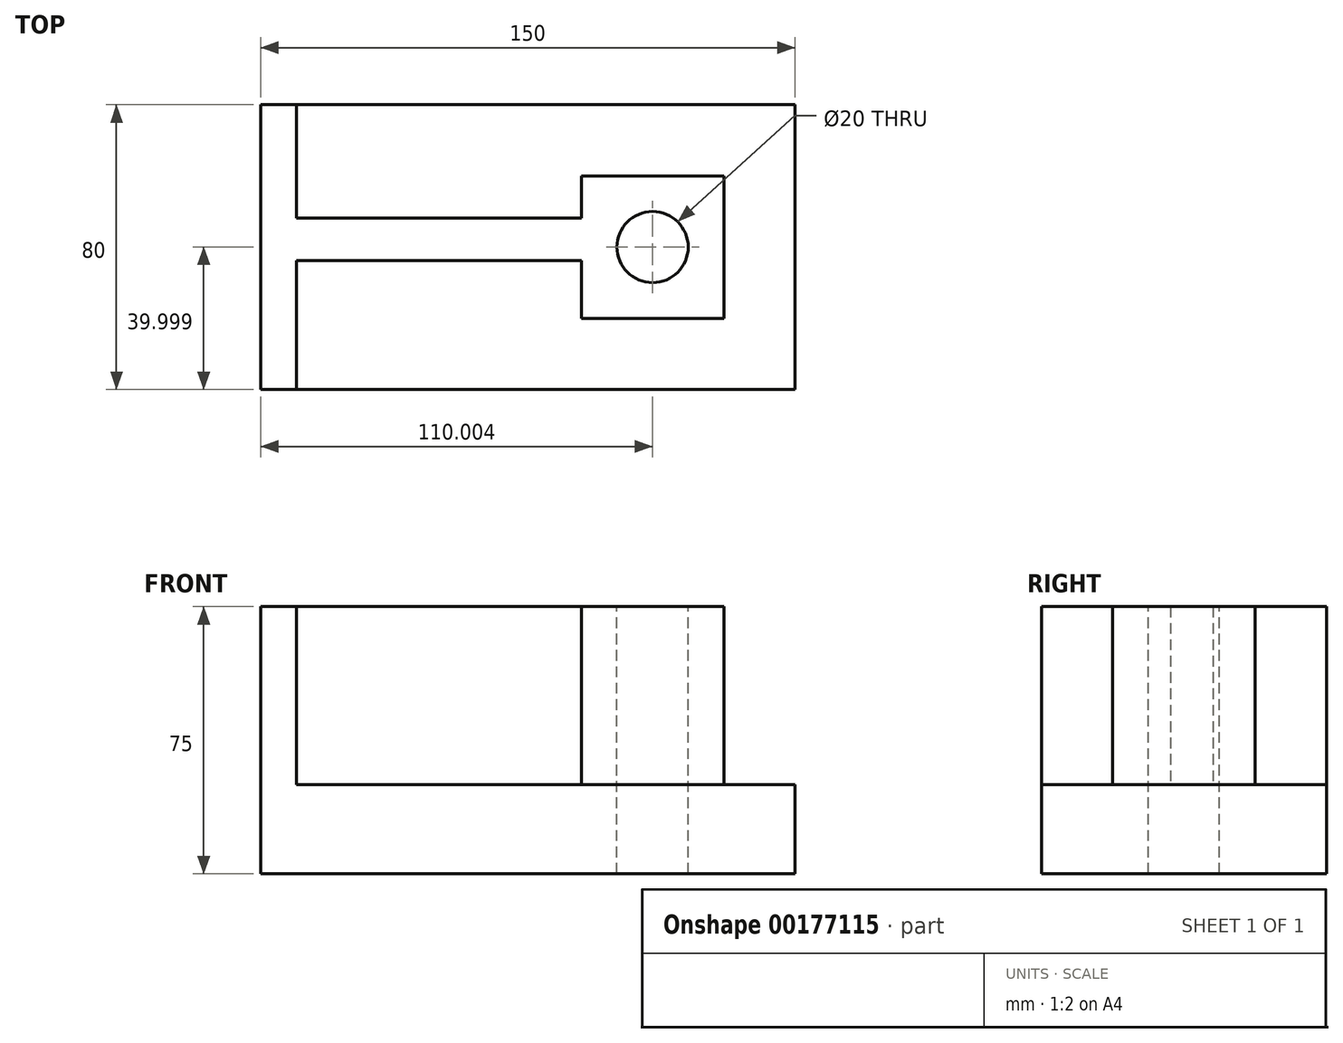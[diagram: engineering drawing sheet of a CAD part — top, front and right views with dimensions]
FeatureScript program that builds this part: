
annotation { "Feature Type Name" : "Feature", "Feature Type Description" : "" }
export const myFeature = defineFeature(function(context is Context, id is Id, definition is map)
    precondition{}
    {
        {
            var Q0;
            Q0=qCreatedBy(makeId("Top.planeOp"),FACE);
            var sketch = newSketch(context, id + "F0", { "sketchPlane" : qUnion([Q0])});
            skLineSegment(sketch, "E0.bottom", {"start": v(-84.32, -48.18) * mm, "end": v(65.68, -48.18) * mm});
            skLineSegment(sketch, "E0.top", {"start": v(-84.32, 31.82) * mm, "end": v(65.68, 31.82) * mm});
            skLineSegment(sketch, "E0.left", {"start": v(-84.32, -48.18) * mm, "end": v(-84.32, 31.82) * mm});
            skLineSegment(sketch, "E0.right", {"start": v(65.68, -48.18) * mm, "end": v(65.68, 31.82) * mm});
            skSolve(sketch);
        }
        {
            var Q0;
            Q0 = qSketchRegion(id + "F0", true);
            extrude(context, id + "F1", {"entities" : qUnion([Q0]), "depth" : 25 * mm});
        }
        {
            var Q0;
            Q0=makeQuery(id+"F1.opExtrude","CAP_FACE",FACE,{"disambiguationData":[OSD([sQuery(id+"F0.wireOp",EDGE,"E0.bottom"),sQuery(id+"F0.wireOp",EDGE,"E0.top"),sQuery(id+"F0.wireOp",EDGE,"E0.left"),sQuery(id+"F0.wireOp",EDGE,"E0.right")])],"isStart":false});
            var sketch = newSketch(context, id + "F2", { "sketchPlane" : qUnion([Q0])});
            skLineSegment(sketch, "E1", {"start": v(45.68, 11.82) * mm, "end": v(5.68, 11.82) * mm});
            skLineSegment(sketch, "E2", {"start": v(5.68, 11.82) * mm, "end": v(5.68, -28.18) * mm});
            skLineSegment(sketch, "E3", {"start": v(5.68, -28.18) * mm, "end": v(45.68, -28.18) * mm});
            skLineSegment(sketch, "E4", {"start": v(45.68, -28.18) * mm, "end": v(45.68, 11.82) * mm});
            skSolve(sketch);
        }
        {
            var Q0;
            Q0=makeQuery(id+"F2.imprint","IMPRINT",FACE,{"disambiguationData":[TD([[makeQuery(id+"F2.imprint","IMPRINT",EDGE,{"derivedFrom":sQuery(id+"F2.wireOp",EDGE,"E1")}),1.0]])]});
            extrude(context, id + "F3", {"entities" : qUnion([Q0]), "operationType" : NewBodyOperationType.ADD, "depth" : 50 * mm});
        }
        {
            var Q0;
            Q0=makeQuery(id+"F3.opExtrude","CAP_FACE",FACE,{"disambiguationData":[OSD([sQuery(id+"F2.wireOp",EDGE,"E1"),sQuery(id+"F2.wireOp",EDGE,"E2"),sQuery(id+"F2.wireOp",EDGE,"E3"),sQuery(id+"F2.wireOp",EDGE,"E4")])],"isStart":false});
            var sketch = newSketch(context, id + "F4", { "sketchPlane" : qUnion([Q0])});
            skCircle(sketch, "E5", {"center": v(25.68, -8.18) * mm, "radius": 10 * mm});
            skPoint(sketch, "E6.end.orphan", {"position": v(45.68, -8.18) * mm});
            skSolve(sketch);
        }
        {
            var Q0;
            Q0=makeQuery(id+"F4.imprint","IMPRINT",FACE,{"disambiguationData":[TD([[makeQuery(id+"F4.imprint","IMPRINT",EDGE,{"derivedFrom":sQuery(id+"F4.wireOp",EDGE,"E5")}),1.0]])]});
            extrude(context, id + "F5", {"entities" : qUnion([Q0]), "operationType" : NewBodyOperationType.REMOVE, "oppositeDirection" : true, "depth" : 75 * mm});
        }
        {
            var Q0;
            Q0=makeQuery(id+"F1.opExtrude","CAP_FACE",FACE,{"disambiguationData":[OSD([sQuery(id+"F0.wireOp",EDGE,"E0.bottom"),sQuery(id+"F0.wireOp",EDGE,"E0.top"),sQuery(id+"F0.wireOp",EDGE,"E0.left"),sQuery(id+"F0.wireOp",EDGE,"E0.right")])],"isStart":false});
            var sketch = newSketch(context, id + "F6", { "sketchPlane" : qUnion([Q0])});
            skLineSegment(sketch, "E7", {"start": v(-74.32, 0) * mm, "end": v(-74.32, -12) * mm});
            skLineSegment(sketch, "E8", {"start": v(-74.32, -12) * mm, "end": v(5.68, -12) * mm});
            skLineSegment(sketch, "E9", {"start": v(5.68, -12) * mm, "end": v(5.68, -8.18) * mm});
            skLineSegment(sketch, "E10", {"start": v(-74.32, 0) * mm, "end": v(5.68, 0) * mm});
            skSolve(sketch);
        }
        {
            var Q0;
            Q0=makeQuery(id+"F6.imprint","IMPRINT",FACE,{"disambiguationData":[TD([[makeQuery(id+"F6.imprint","IMPRINT",EDGE,{"derivedFrom":sQuery(id+"F6.wireOp",EDGE,"E7")}),1.0]])]});
            extrude(context, id + "F7", {"entities" : qUnion([Q0]), "operationType" : NewBodyOperationType.ADD, "depth" : 50 * mm});
        }
        {
            var Q0;
            Q0=makeQuery(id+"F1.opExtrude","CAP_FACE",FACE,{"disambiguationData":[OSD([sQuery(id+"F0.wireOp",EDGE,"E0.bottom"),sQuery(id+"F0.wireOp",EDGE,"E0.top"),sQuery(id+"F0.wireOp",EDGE,"E0.left"),sQuery(id+"F0.wireOp",EDGE,"E0.right")])],"isStart":false});
            var sketch = newSketch(context, id + "F8", { "sketchPlane" : qUnion([Q0])});
            skLineSegment(sketch, "E11", {"start": v(-84.32, -48.18) * mm, "end": v(-74.32, -48.18) * mm});
            skLineSegment(sketch, "E12", {"start": v(-74.32, -48.18) * mm, "end": v(-74.32, 31.82) * mm});
            skLineSegment(sketch, "E13", {"start": v(-74.32, 31.82) * mm, "end": v(-84.32, 31.82) * mm});
            skLineSegment(sketch, "E14", {"start": v(-84.32, 31.82) * mm, "end": v(-94.32, 31.82) * mm});
            skLineSegment(sketch, "E15", {"start": v(-94.32, 31.82) * mm, "end": v(-94.32, -48.18) * mm});
            skLineSegment(sketch, "E16", {"start": v(-94.32, -48.18) * mm, "end": v(-84.32, -48.18) * mm});
            skSolve(sketch);
        }
        {
            var Q0;
            {var subQ4=sQuery(id+"F8.wireOp",EDGE,"E11");Q0=makeQuery(id+"F8.imprint","IMPRINT",FACE,{"disambiguationData":[TD([[makeQuery(id+"F8.imprint","IMPRINT",EDGE,{"derivedFrom":subQ4}),1.0]])]});}
            extrude(context, id + "F9", {"entities" : qUnion([Q0]), "operationType" : NewBodyOperationType.ADD, "depth" : 50 * mm});
        }
    });
